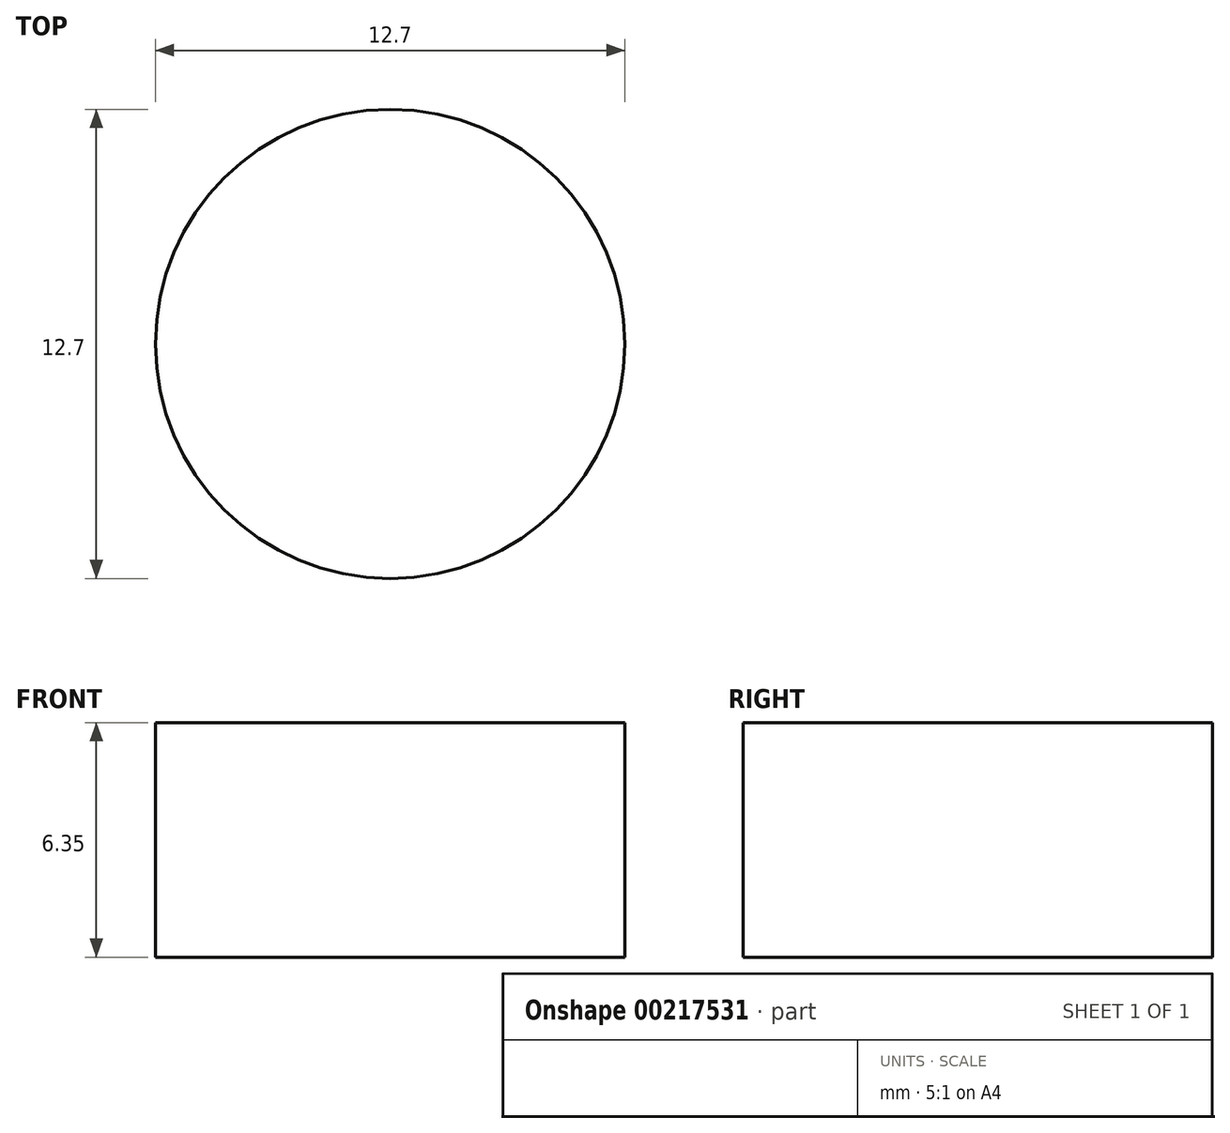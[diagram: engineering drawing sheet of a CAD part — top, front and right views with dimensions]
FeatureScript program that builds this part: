
annotation { "Feature Type Name" : "Feature", "Feature Type Description" : "" }
export const myFeature = defineFeature(function(context is Context, id is Id, definition is map)
    precondition{}
    {
        {
            var Q0;
            Q0=qCreatedBy(makeId("Top.planeOp"),FACE);
            var sketch = newSketch(context, id + "F0", { "sketchPlane" : qUnion([Q0])});
            skCircle(sketch, "E0", {"center": v(0, 0) * mm, "radius": 6.35 * mm});
            skSolve(sketch);
        }
        {
            var Q0;
            Q0 = qSketchRegion(id + "F0", true);
            extrude(context, id + "F1", {"entities" : qUnion([Q0]), "depth" : 6.35 * mm});
        }
    });
